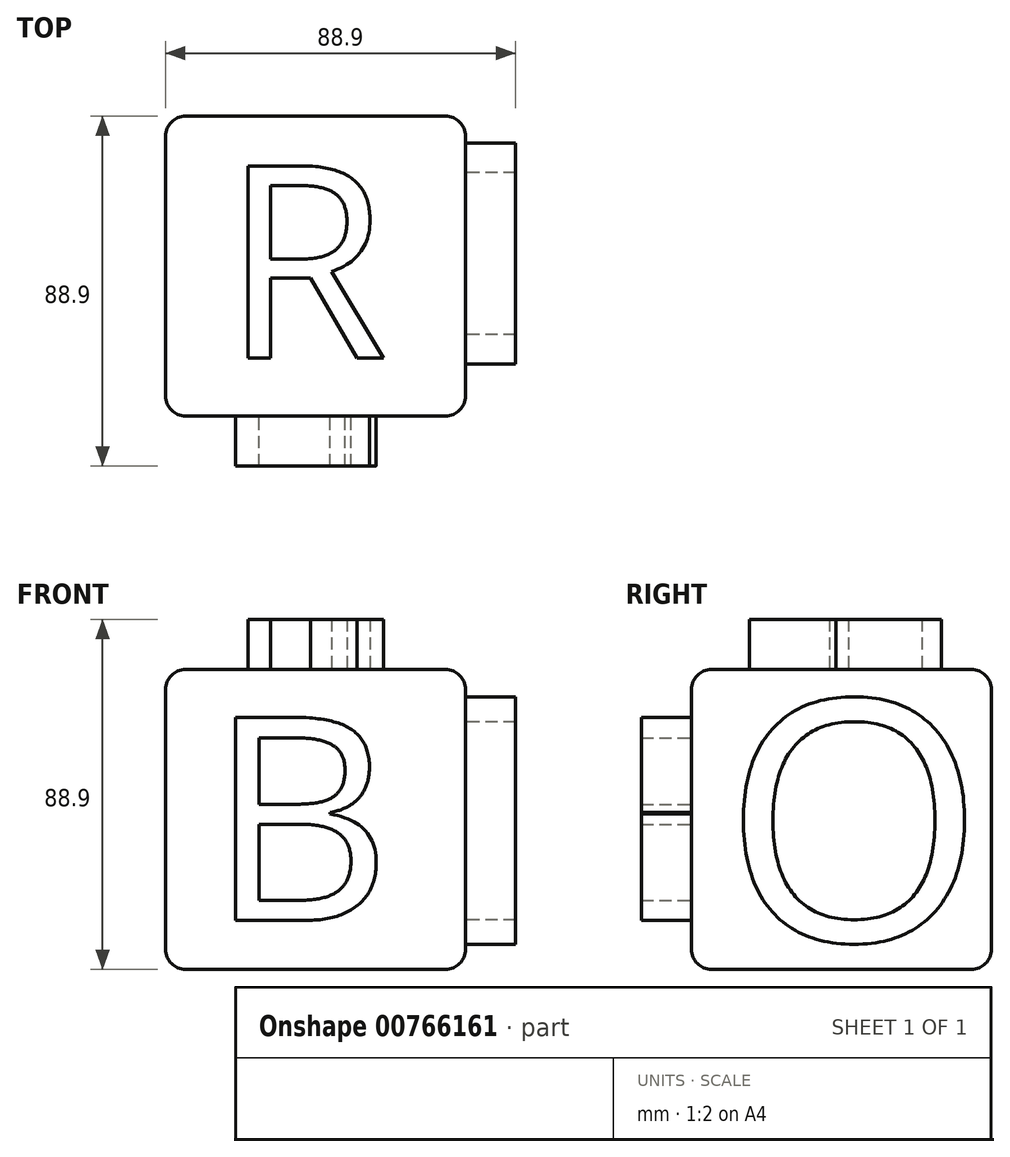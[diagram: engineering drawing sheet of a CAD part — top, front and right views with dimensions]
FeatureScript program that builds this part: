
annotation { "Feature Type Name" : "Feature", "Feature Type Description" : "" }
export const myFeature = defineFeature(function(context is Context, id is Id, definition is map)
    precondition{}
    {
        {
            var Q0;
            Q0=qCreatedBy(makeId("Front.planeOp"),FACE);
            var sketch = newSketch(context, id + "F0", { "sketchPlane" : qUnion([Q0])});
            skLineSegment(sketch, "E0.bottom", {"start": v(-73.76, 76.2) * mm, "end": v(2.44, 76.2) * mm});
            skLineSegment(sketch, "E0.top", {"start": v(-73.76, 0) * mm, "end": v(2.44, 0) * mm});
            skLineSegment(sketch, "E0.left", {"start": v(-73.76, 76.2) * mm, "end": v(-73.76, 0) * mm});
            skLineSegment(sketch, "E0.right", {"start": v(2.44, 76.2) * mm, "end": v(2.44, 0) * mm});
            skSolve(sketch);
        }
        {
            var Q0;
            Q0=makeQuery(id+"F0.imprint","IMPRINT",FACE,{"disambiguationData":[TD([[makeQuery(id+"F0.imprint","IMPRINT",EDGE,{"derivedFrom":sQuery(id+"F0.wireOp",EDGE,"E0.bottom")}),-1.0]])]});
            extrude(context, id + "F1", {"entities" : qUnion([Q0]), "depth" : 76.2 * mm, "offsetDistance" : 25.4 * mm});
        }
        {
            var Q0;
            Q0=makeQuery(id+"F1.opExtrude","SWEPT_FACE",FACE,{"disambiguationData":[OSD([sQuery(id+"F0.wireOp",EDGE,"E0.left")])]});
            var Q1;
            Q1=makeQuery(id+"F1.opExtrude","SWEPT_FACE",FACE,{"disambiguationData":[OSD([sQuery(id+"F0.wireOp",EDGE,"E0.top")])]});
            var Q2;
            Q2=makeQuery(id+"F1.opExtrude","CAP_FACE",FACE,{"disambiguationData":[OSD([sQuery(id+"F0.wireOp",EDGE,"E0.bottom"),sQuery(id+"F0.wireOp",EDGE,"E0.top"),sQuery(id+"F0.wireOp",EDGE,"E0.left"),sQuery(id+"F0.wireOp",EDGE,"E0.right")])],"isStart":false});
            var Q3;
            Q3=makeQuery(id+"F1.opExtrude","SWEPT_FACE",FACE,{"disambiguationData":[OSD([sQuery(id+"F0.wireOp",EDGE,"E0.right")])]});
            var Q4;
            Q4=makeQuery(id+"F1.opExtrude","SWEPT_FACE",FACE,{"disambiguationData":[OSD([sQuery(id+"F0.wireOp",EDGE,"E0.bottom")])]});
            var Q5;
            Q5=makeQuery(id+"F1.opExtrude","CAP_FACE",FACE,{"disambiguationData":[OSD([sQuery(id+"F0.wireOp",EDGE,"E0.bottom"),sQuery(id+"F0.wireOp",EDGE,"E0.top"),sQuery(id+"F0.wireOp",EDGE,"E0.left"),sQuery(id+"F0.wireOp",EDGE,"E0.right")])],"isStart":true});
            fillet(context, id + "F2", {"entities" : qUnion([Q0, Q1, Q2, Q3, Q4, Q5]), "radius" : 5.08 * mm, "tangentPropagation" : true, "allowEdgeOverflow" : false});
        }
        {
            var Q0;
            Q0=makeQuery(id+"F1.opExtrude","SWEPT_FACE",FACE,{"disambiguationData":[OSD([sQuery(id+"F0.wireOp",EDGE,"E0.bottom")])]});
            var sketch = newSketch(context, id + "F3", { "sketchPlane" : qUnion([Q0])});
            skText(sketch, "E1", { "text": "R", "fontName": "OpenSans-Regular.ttf"});
            const initialGuessF3  = {"E1": [-0.05952, -0.06152, 1, 0, 0.04929]};
            skSetInitialGuess(sketch, initialGuessF3);
            skSolve(sketch);
        }
        {
            var Q0;
            Q0 = qSketchRegion(id + "F3", true);
            extrude(context, id + "F4", {"entities" : qUnion([Q0]), "operationType" : NewBodyOperationType.ADD, "depth" : 12.7 * mm, "offsetDistance" : 25.4 * mm});
        }
        {
            var Q0;
            Q0=makeQuery(id+"F1.opExtrude","SWEPT_FACE",FACE,{"disambiguationData":[OSD([sQuery(id+"F0.wireOp",EDGE,"E0.right")])]});
            var sketch = newSketch(context, id + "F5", { "sketchPlane" : qUnion([Q0])});
            skText(sketch, "E2", { "text": "O", "fontName": "OpenSans-Regular.ttf"});
            const initialGuessF5  = {"E2": [-0.06824, 0.00723, 1, 0, 0.0616]};
            skSetInitialGuess(sketch, initialGuessF5);
            skSolve(sketch);
        }
        {
            var Q0;
            Q0=makeQuery(id+"F5.imprint","IMPRINT",FACE,{"disambiguationData":[TD([[makeQuery(id+"F5.imprint","IMPRINT",EDGE,{"derivedFrom":sQuery(id+"F5.wireOp",EDGE,"E2.sketch_text.stroke-0")}),-1.0]])]});
            extrude(context, id + "F6", {"entities" : qUnion([Q0]), "operationType" : NewBodyOperationType.ADD, "depth" : 12.7 * mm, "offsetDistance" : 25.4 * mm});
        }
        {
            var Q0;
            Q0=makeQuery(id+"F1.opExtrude","CAP_FACE",FACE,{"disambiguationData":[OSD([sQuery(id+"F0.wireOp",EDGE,"E0.bottom"),sQuery(id+"F0.wireOp",EDGE,"E0.top"),sQuery(id+"F0.wireOp",EDGE,"E0.left"),sQuery(id+"F0.wireOp",EDGE,"E0.right")])],"isStart":false});
            var sketch = newSketch(context, id + "F7", { "sketchPlane" : qUnion([Q0])});
            skText(sketch, "E3", { "text": "B", "fontName": "OpenSans-Regular.ttf"});
            const initialGuessF7  = {"E3": [-0.0631, 0.01246, 1, 0, 0.05205]};
            skSetInitialGuess(sketch, initialGuessF7);
            skSolve(sketch);
        }
        {
            var Q0;
            Q0=makeQuery(id+"F7.imprint","IMPRINT",FACE,{"disambiguationData":[TD([[makeQuery(id+"F7.imprint","IMPRINT",EDGE,{"derivedFrom":sQuery(id+"F7.wireOp",EDGE,"E3.sketch_text.stroke-0")}),-1.0]])]});
            extrude(context, id + "F8", {"entities" : qUnion([Q0]), "operationType" : NewBodyOperationType.ADD, "depth" : 12.7 * mm, "offsetDistance" : 25.4 * mm});
        }
    });
